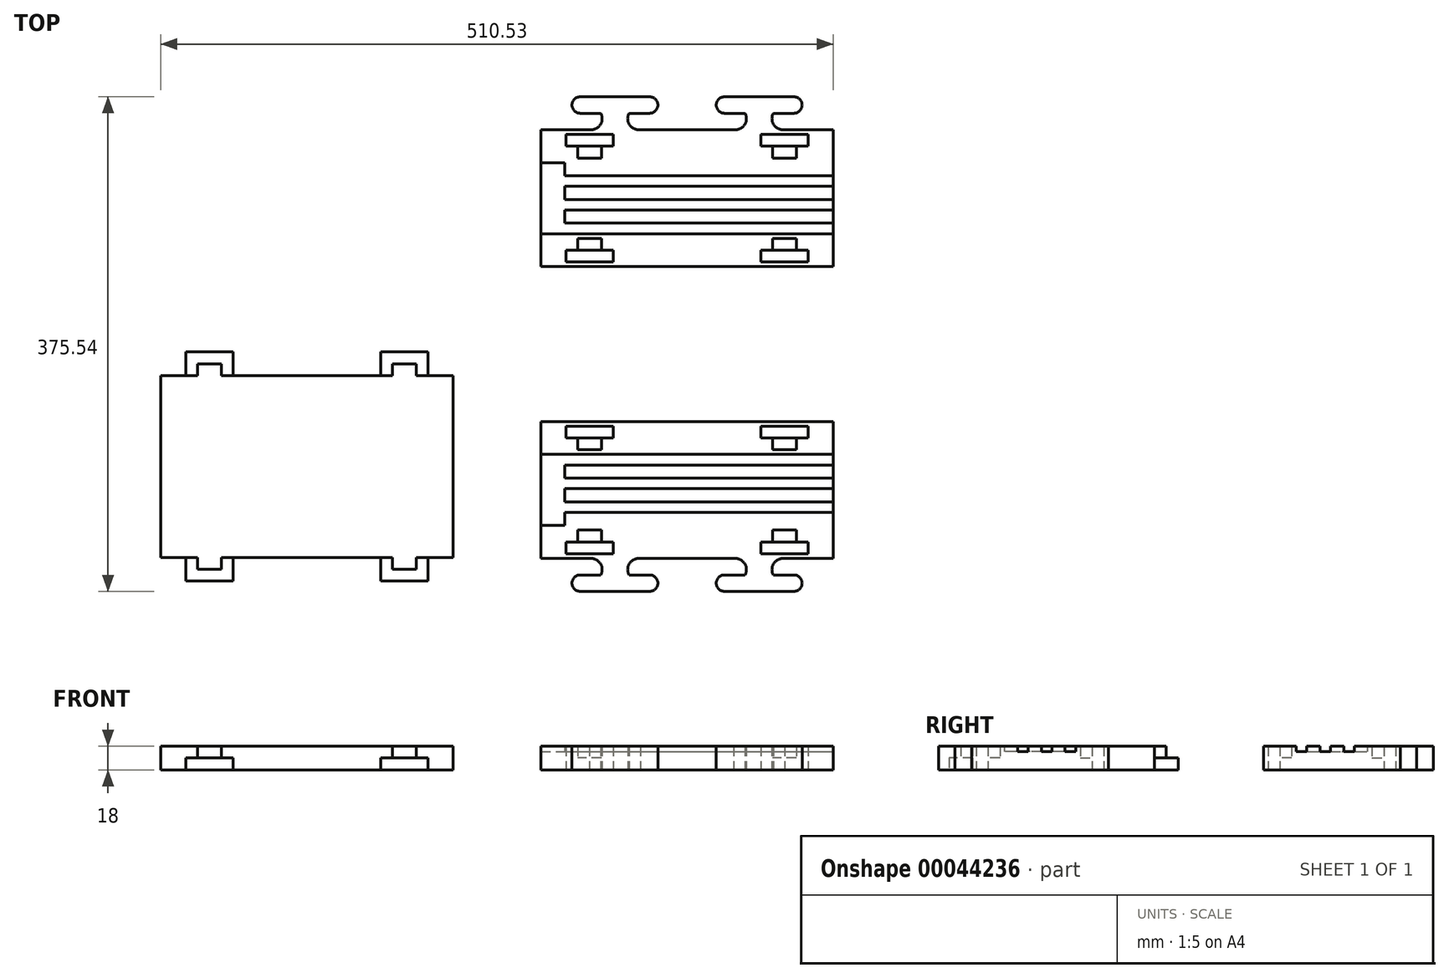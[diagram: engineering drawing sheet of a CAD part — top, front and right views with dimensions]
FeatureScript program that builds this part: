
annotation { "Feature Type Name" : "Feature", "Feature Type Description" : "" }
export const myFeature = defineFeature(function(context is Context, id is Id, definition is map)
    precondition{}
    {
        {
            var Q0;
            Q0=qCreatedBy(makeId("Top.planeOp"),FACE);
            var sketch = newSketch(context, id + "F0", { "sketchPlane" : qUnion([Q0])});
            skLineSegment(sketch, "E0.bottom", {"start": v(102.08, 91.5) * mm, "end": v(176.08, 91.5) * mm});
            skLineSegment(sketch, "E0.left", {"start": v(28.08, 91.5) * mm, "end": v(28.08, -12.5) * mm});
            skLineSegment(sketch, "E0.right", {"start": v(250.08, 91.5) * mm, "end": v(250.08, -12.5) * mm});
            skPoint(sketch, "E1", {"position": v(28.08, 66.5) * mm});
            skPoint(sketch, "E2", {"position": v(28.08, 12.5) * mm});
            skPoint(sketch, "E3", {"position": v(28.08, 58.5) * mm});
            skPoint(sketch, "E4", {"position": v(28.08, 22.5) * mm});
            skPoint(sketch, "E5", {"position": v(28.08, 48.5) * mm});
            skPoint(sketch, "E6", {"position": v(29.26, 40.5) * mm});
            skPoint(sketch, "E7", {"position": v(28.08, 30.5) * mm});
            skLineSegment(sketch, "E8", {"start": v(28.08, 66.5) * mm, "end": v(250.08, 66.5) * mm});
            skLineSegment(sketch, "E9", {"start": v(28.08, 48.5) * mm, "end": v(250.08, 48.5) * mm});
            skLineSegment(sketch, "E10", {"start": v(28.08, 30.5) * mm, "end": v(250.08, 30.5) * mm});
            skLineSegment(sketch, "E11", {"start": v(28.08, 12.5) * mm, "end": v(250.08, 12.5) * mm});
            skPoint(sketch, "E12", {"position": v(102.08, 91.5) * mm});
            skPoint(sketch, "E13", {"position": v(176.08, 91.5) * mm});
            skLineSegment(sketch, "E14", {"start": v(102.08, 91.5) * mm, "end": v(102.08, -12.5) * mm, "construction": true});
            skLineSegment(sketch, "E15", {"start": v(176.08, 91.5) * mm, "end": v(176.08, -12.5) * mm, "construction": true});
            skPoint(sketch, "E16", {"position": v(46.08, 66.5) * mm});
            skLineSegment(sketch, "E17", {"start": v(46.08, 66.5) * mm, "end": v(46.08, 12.5) * mm, "construction": true});
            skPoint(sketch, "E18", {"position": v(46.08, 58.5) * mm});
            skPoint(sketch, "E19", {"position": v(46.08, 40.5) * mm});
            skPoint(sketch, "E20", {"position": v(46.08, 22.5) * mm});
            skLineSegment(sketch, "E21", {"start": v(46.08, 40.5) * mm, "end": v(250.08, 40.5) * mm});
            skLineSegment(sketch, "E22", {"start": v(46.08, 58.5) * mm, "end": v(250.08, 58.5) * mm});
            skLineSegment(sketch, "E23", {"start": v(46.08, 22.5) * mm, "end": v(250.08, 22.5) * mm});
            skLineSegment(sketch, "E24", {"start": v(28.08, -12.5) * mm, "end": v(67.03, -12.5) * mm});
            skLineSegment(sketch, "E25", {"start": v(250.08, 91.5) * mm, "end": v(176.08, 91.5) * mm});
            skLineSegment(sketch, "E26", {"start": v(102.08, 91.5) * mm, "end": v(28.08, 91.5) * mm});
            skPoint(sketch, "E27", {"position": v(213.08, 91.5) * mm});
            skPoint(sketch, "E28", {"position": v(65.08, 91.5) * mm});
            skLineSegment(sketch, "E29", {"start": v(65.08, 91.5) * mm, "end": v(65.08, -12.5) * mm, "construction": true});
            skLineSegment(sketch, "E30", {"start": v(213.08, 91.5) * mm, "end": v(213.08, -12.5) * mm, "construction": true});
            skPoint(sketch, "E31", {"position": v(65.08, -9) * mm});
            skPoint(sketch, "E32", {"position": v(65.08, 88) * mm});
            skPoint(sketch, "E33", {"position": v(213.08, 88) * mm});
            skPoint(sketch, "E34", {"position": v(213.08, -9) * mm});
            skLineSegment(sketch, "E35", {"start": v(213.08, -9) * mm, "end": v(231.08, -9) * mm});
            skLineSegment(sketch, "E36", {"start": v(213.08, -9) * mm, "end": v(195.08, -9) * mm});
            skLineSegment(sketch, "E37", {"start": v(213.08, 88) * mm, "end": v(195.08, 88) * mm});
            skLineSegment(sketch, "E38", {"start": v(213.08, 88) * mm, "end": v(231.08, 88) * mm});
            skLineSegment(sketch, "E39", {"start": v(65.08, 88) * mm, "end": v(83.08, 88) * mm});
            skLineSegment(sketch, "E40", {"start": v(65.08, 88) * mm, "end": v(47.08, 88) * mm});
            skLineSegment(sketch, "E41", {"start": v(65.08, -9) * mm, "end": v(47.08, -9) * mm});
            skLineSegment(sketch, "E42", {"start": v(65.08, -9) * mm, "end": v(83.08, -9) * mm});
            skLineSegment(sketch, "E43", {"start": v(195.08, -9) * mm, "end": v(195.08, 0) * mm});
            skLineSegment(sketch, "E44", {"start": v(195.08, 88) * mm, "end": v(195.08, 79) * mm});
            skLineSegment(sketch, "E45", {"start": v(83.08, 88) * mm, "end": v(83.08, 79) * mm});
            skLineSegment(sketch, "E46", {"start": v(83.08, -9) * mm, "end": v(83.08, 0) * mm});
            skLineSegment(sketch, "E47", {"start": v(195.08, 0) * mm, "end": v(231.08, 0) * mm});
            skLineSegment(sketch, "E48", {"start": v(231.08, 0) * mm, "end": v(231.08, -9) * mm});
            skLineSegment(sketch, "E49", {"start": v(195.08, 79) * mm, "end": v(231.08, 79) * mm});
            skLineSegment(sketch, "E50", {"start": v(231.08, 79) * mm, "end": v(231.08, 88) * mm});
            skLineSegment(sketch, "E51", {"start": v(83.08, 79) * mm, "end": v(47.08, 79) * mm});
            skLineSegment(sketch, "E52", {"start": v(47.08, 79) * mm, "end": v(47.08, 88) * mm});
            skLineSegment(sketch, "E53", {"start": v(47.08, -9) * mm, "end": v(47.08, 0) * mm});
            skLineSegment(sketch, "E54", {"start": v(47.08, 0) * mm, "end": v(83.08, 0) * mm});
            skPoint(sketch, "E55", {"position": v(65.08, 70) * mm});
            skPoint(sketch, "E56", {"position": v(65.08, 9) * mm});
            skPoint(sketch, "E57", {"position": v(213.08, 9) * mm});
            skPoint(sketch, "E58", {"position": v(213.08, 70) * mm});
            skLineSegment(sketch, "E59", {"start": v(213.08, 9) * mm, "end": v(222.08, 9) * mm});
            skLineSegment(sketch, "E60", {"start": v(213.08, 9) * mm, "end": v(204.08, 9) * mm});
            skLineSegment(sketch, "E61", {"start": v(213.08, 70) * mm, "end": v(222.08, 70) * mm});
            skLineSegment(sketch, "E62", {"start": v(213.08, 70) * mm, "end": v(204.08, 70) * mm});
            skLineSegment(sketch, "E63", {"start": v(65.08, 70) * mm, "end": v(74.08, 70) * mm});
            skLineSegment(sketch, "E64", {"start": v(65.08, 70) * mm, "end": v(56.08, 70) * mm});
            skLineSegment(sketch, "E65", {"start": v(65.08, 9) * mm, "end": v(74.08, 9) * mm});
            skLineSegment(sketch, "E66", {"start": v(65.08, 9) * mm, "end": v(56.08, 9) * mm});
            skLineSegment(sketch, "E67", {"start": v(222.08, 9) * mm, "end": v(222.08, 0) * mm});
            skLineSegment(sketch, "E68", {"start": v(204.08, 9) * mm, "end": v(204.08, 0) * mm});
            skLineSegment(sketch, "E69", {"start": v(222.08, 70) * mm, "end": v(222.08, 79) * mm});
            skLineSegment(sketch, "E70", {"start": v(204.08, 70) * mm, "end": v(204.08, 79) * mm});
            skLineSegment(sketch, "E71", {"start": v(74.08, 70) * mm, "end": v(74.08, 79) * mm});
            skLineSegment(sketch, "E72", {"start": v(56.08, 70) * mm, "end": v(56.08, 79) * mm});
            skLineSegment(sketch, "E73", {"start": v(74.08, 9) * mm, "end": v(74.08, 0) * mm});
            skLineSegment(sketch, "E74", {"start": v(56.08, 9) * mm, "end": v(56.08, 0) * mm});
            skLineSegment(sketch, "E75", {"start": v(46.08, 58.5) * mm, "end": v(46.08, 48.5) * mm});
            skLineSegment(sketch, "E76", {"start": v(46.08, 40.5) * mm, "end": v(46.08, 30.5) * mm});
            skLineSegment(sketch, "E77", {"start": v(46.08, 22.5) * mm, "end": v(46.08, 12.5) * mm});
            skPoint(sketch, "E78", {"position": v(139.08, 91.5) * mm});
            skLineSegment(sketch, "E79", {"start": v(139.08, 91.5) * mm, "end": v(139.08, -12.5) * mm, "construction": true});
            skLineSegment(sketch, "E80.trimOffspring", {"start": v(119.85, -12.5) * mm, "end": v(158.31, -12.5) * mm});
            skLineSegment(sketch, "E81.trimOffspring", {"start": v(211.13, -12.5) * mm, "end": v(250.08, -12.5) * mm});
            skLineSegment(sketch, "E82", {"start": v(101.6, -12.5) * mm, "end": v(102.08, -12.5) * mm});
            skLineSegment(sketch, "E83", {"start": v(119.85, -12.5) * mm, "end": v(102.08, -12.5) * mm});
            skLineSegment(sketch, "E84", {"start": v(158.31, -12.5) * mm, "end": v(176.08, -12.5) * mm});
            skLineSegment(sketch, "E85", {"start": v(176.57, -12.5) * mm, "end": v(176.08, -12.5) * mm});
            skLineSegment(sketch, "E86", {"start": v(193.85, -12.5) * mm, "end": v(193.85, -37.5) * mm, "construction": true});
            skLineSegment(sketch, "E87", {"start": v(84.31, -12.5) * mm, "end": v(84.31, -37.5) * mm, "construction": true});
            skLineSegment(sketch, "E88", {"start": v(84.31, -25) * mm, "end": v(193.85, -25) * mm, "construction": true});
            skLineSegment(sketch, "E89", {"start": v(84.31, -25) * mm, "end": v(31.64, -25) * mm, "construction": true});
            skLineSegment(sketch, "E90", {"start": v(193.85, -25) * mm, "end": v(246.52, -25) * mm, "construction": true});
            skArc(sketch, "E91", {"start": v(213.08, -12.5) * mm, "mid": v(205.04, -16.17) * mm, "end": v(204.52, -25) * mm});
            skArc(sketch, "E92.MirrorCS", {"start": v(174.62, -12.5) * mm, "mid": v(182.66, -16.17) * mm, "end": v(183.17, -25) * mm});
            skArc(sketch, "E93.MirrorCS", {"start": v(103.55, -12.5) * mm, "mid": v(95.5, -16.17) * mm, "end": v(94.99, -25) * mm});
            skArc(sketch, "E94.MirrorCS", {"start": v(65.08, -12.5) * mm, "mid": v(73.13, -16.17) * mm, "end": v(73.64, -25) * mm});
            skLineSegment(sketch, "E95", {"start": v(73.64, -25) * mm, "end": v(57.98, -25) * mm});
            skLineSegment(sketch, "E96", {"start": v(94.99, -25) * mm, "end": v(110.65, -25) * mm});
            skLineSegment(sketch, "E97", {"start": v(183.17, -25) * mm, "end": v(167.51, -25) * mm});
            skLineSegment(sketch, "E98", {"start": v(204.52, -25) * mm, "end": v(220.18, -25) * mm});
            skArc(sketch, "E99", {"start": v(57.98, -25) * mm, "mid": v(51.73, -31.25) * mm, "end": v(57.98, -37.5) * mm});
            skArc(sketch, "E100.MirrorCS", {"start": v(110.65, -25) * mm, "mid": v(116.9, -31.25) * mm, "end": v(110.65, -37.5) * mm});
            skArc(sketch, "E101.MirrorCS", {"start": v(167.51, -25) * mm, "mid": v(161.26, -31.25) * mm, "end": v(167.51, -37.5) * mm});
            skArc(sketch, "E102.MirrorCS", {"start": v(220.18, -25) * mm, "mid": v(226.43, -31.25) * mm, "end": v(220.18, -37.5) * mm});
            skLineSegment(sketch, "E103", {"start": v(57.98, -37.5) * mm, "end": v(110.65, -37.5) * mm});
            skLineSegment(sketch, "E104", {"start": v(167.51, -37.5) * mm, "end": v(220.18, -37.5) * mm});
            skLineSegment(sketch, "E105", {"start": v(-11.33, 150.27) * mm, "end": v(328.55, 150.27) * mm});
            skLineSegment(sketch, "E106.MirrorCS", {"start": v(176.57, 313.04) * mm, "end": v(176.08, 313.04) * mm});
            skLineSegment(sketch, "E107.MirrorCS", {"start": v(231.08, 221.54) * mm, "end": v(231.08, 212.54) * mm});
            skLineSegment(sketch, "E108.MirrorCS", {"start": v(213.08, 230.54) * mm, "end": v(204.08, 230.54) * mm});
            skLineSegment(sketch, "E109.MirrorCS", {"start": v(83.08, 212.54) * mm, "end": v(83.08, 221.54) * mm});
            skLineSegment(sketch, "E110.MirrorCS", {"start": v(65.08, 291.54) * mm, "end": v(56.08, 291.54) * mm});
            skLineSegment(sketch, "E111.MirrorCS", {"start": v(47.08, 221.54) * mm, "end": v(47.08, 212.54) * mm});
            skLineSegment(sketch, "E112.MirrorCS", {"start": v(195.08, 212.54) * mm, "end": v(195.08, 221.54) * mm});
            skLineSegment(sketch, "E113.MirrorCS", {"start": v(213.08, 291.54) * mm, "end": v(204.08, 291.54) * mm});
            skLineSegment(sketch, "E114.MirrorCS", {"start": v(65.08, 230.54) * mm, "end": v(56.08, 230.54) * mm});
            skLineSegment(sketch, "E115.MirrorCS", {"start": v(74.08, 291.54) * mm, "end": v(74.08, 300.54) * mm});
            skLineSegment(sketch, "E116.MirrorCS", {"start": v(65.08, 291.54) * mm, "end": v(74.08, 291.54) * mm});
            skLineSegment(sketch, "E117.MirrorCS", {"start": v(204.08, 291.54) * mm, "end": v(204.08, 300.54) * mm});
            skLineSegment(sketch, "E118.MirrorCS", {"start": v(213.08, 230.54) * mm, "end": v(222.08, 230.54) * mm});
            skLineSegment(sketch, "E119.MirrorCS", {"start": v(46.08, 242.04) * mm, "end": v(46.08, 252.04) * mm});
            skLineSegment(sketch, "E120.MirrorCS", {"start": v(83.08, 309.54) * mm, "end": v(83.08, 300.54) * mm});
            skLineSegment(sketch, "E121.MirrorCS", {"start": v(222.08, 291.54) * mm, "end": v(222.08, 300.54) * mm});
            skLineSegment(sketch, "E122.MirrorCS", {"start": v(46.08, 278.04) * mm, "end": v(46.08, 288.04) * mm});
            skLineSegment(sketch, "E123.MirrorCS", {"start": v(46.08, 260.04) * mm, "end": v(46.08, 270.04) * mm});
            skLineSegment(sketch, "E124.MirrorCS", {"start": v(56.08, 291.54) * mm, "end": v(56.08, 300.54) * mm});
            skLineSegment(sketch, "E125.MirrorCS", {"start": v(65.08, 230.54) * mm, "end": v(74.08, 230.54) * mm});
            skLineSegment(sketch, "E126.MirrorCS", {"start": v(46.08, 234.04) * mm, "end": v(46.08, 288.04) * mm, "construction": true});
            skLineSegment(sketch, "E127.MirrorCS", {"start": v(213.08, 291.54) * mm, "end": v(222.08, 291.54) * mm});
            skPoint(sketch, "E128.MirrorP", {"position": v(213.08, 212.54) * mm});
            skLineSegment(sketch, "E129.MirrorCS", {"start": v(250.08, 209.04) * mm, "end": v(250.08, 313.04) * mm});
            skPoint(sketch, "E130.MirrorP", {"position": v(46.08, 234.04) * mm});
            skArc(sketch, "E131.MirrorCS", {"start": v(65.08, 313.04) * mm, "mid": v(73.13, 316.7) * mm, "end": v(73.64, 325.54) * mm});
            skLineSegment(sketch, "E132.MirrorCS", {"start": v(28.08, 252.04) * mm, "end": v(250.08, 252.04) * mm});
            skLineSegment(sketch, "E133.MirrorCS", {"start": v(65.08, 212.54) * mm, "end": v(83.08, 212.54) * mm});
            skLineSegment(sketch, "E134.MirrorCS", {"start": v(167.51, 338.04) * mm, "end": v(220.18, 338.04) * mm});
            skLineSegment(sketch, "E135.MirrorCS", {"start": v(84.31, 325.54) * mm, "end": v(193.85, 325.54) * mm, "construction": true});
            skLineSegment(sketch, "E136.MirrorCS", {"start": v(28.08, 313.04) * mm, "end": v(67.03, 313.04) * mm});
            skArc(sketch, "E137.MirrorCS", {"start": v(103.55, 313.04) * mm, "mid": v(95.5, 316.7) * mm, "end": v(94.99, 325.54) * mm});
            skArc(sketch, "E138.MirrorCS", {"start": v(57.98, 325.54) * mm, "mid": v(51.73, 331.79) * mm, "end": v(57.98, 338.04) * mm});
            skLineSegment(sketch, "E139.MirrorCS", {"start": v(139.08, 209.04) * mm, "end": v(139.08, 313.04) * mm, "construction": true});
            skLineSegment(sketch, "E140.MirrorCS", {"start": v(65.08, 309.54) * mm, "end": v(47.08, 309.54) * mm});
            skPoint(sketch, "E141.MirrorP", {"position": v(28.08, 278.04) * mm});
            skPoint(sketch, "E142.MirrorP", {"position": v(46.08, 278.04) * mm});
            skPoint(sketch, "E143.MirrorP", {"position": v(213.08, 209.04) * mm});
            skPoint(sketch, "E144.MirrorP", {"position": v(213.08, 230.54) * mm});
            skPoint(sketch, "E145.MirrorP", {"position": v(28.08, 270.04) * mm});
            skPoint(sketch, "E146.MirrorP", {"position": v(65.08, 209.04) * mm});
            skPoint(sketch, "E147.MirrorP", {"position": v(28.08, 252.04) * mm});
            skArc(sketch, "E148.MirrorCS", {"start": v(213.08, 313.04) * mm, "mid": v(205.04, 316.7) * mm, "end": v(204.52, 325.54) * mm});
            skPoint(sketch, "E149.MirrorP", {"position": v(65.08, 212.54) * mm});
            skArc(sketch, "E150.MirrorCS", {"start": v(167.51, 325.54) * mm, "mid": v(161.26, 331.79) * mm, "end": v(167.51, 338.04) * mm});
            skLineSegment(sketch, "E151.MirrorCS", {"start": v(119.85, 313.04) * mm, "end": v(158.31, 313.04) * mm});
            skArc(sketch, "E152.MirrorCS", {"start": v(174.62, 313.04) * mm, "mid": v(182.66, 316.7) * mm, "end": v(183.17, 325.54) * mm});
            skLineSegment(sketch, "E153.MirrorCS", {"start": v(176.08, 209.04) * mm, "end": v(176.08, 313.04) * mm, "construction": true});
            skLineSegment(sketch, "E154.MirrorCS", {"start": v(102.08, 209.04) * mm, "end": v(102.08, 313.04) * mm, "construction": true});
            skPoint(sketch, "E155.MirrorP", {"position": v(46.08, 260.04) * mm});
            skLineSegment(sketch, "E156.MirrorCS", {"start": v(213.08, 209.04) * mm, "end": v(213.08, 313.04) * mm, "construction": true});
            skLineSegment(sketch, "E157.MirrorCS", {"start": v(57.98, 338.04) * mm, "end": v(110.65, 338.04) * mm});
            skLineSegment(sketch, "E158.MirrorCS", {"start": v(84.31, 313.04) * mm, "end": v(84.31, 338.04) * mm, "construction": true});
            skArc(sketch, "E159.MirrorCS", {"start": v(220.18, 325.54) * mm, "mid": v(226.43, 331.79) * mm, "end": v(220.18, 338.04) * mm});
            skLineSegment(sketch, "E160.MirrorCS", {"start": v(47.08, 309.54) * mm, "end": v(47.08, 300.54) * mm});
            skPoint(sketch, "E161.MirrorP", {"position": v(65.08, 309.54) * mm});
            skPoint(sketch, "E162.MirrorP", {"position": v(139.08, 209.04) * mm});
            skLineSegment(sketch, "E163.MirrorCS", {"start": v(183.17, 325.54) * mm, "end": v(167.51, 325.54) * mm});
            skPoint(sketch, "E164.MirrorP", {"position": v(65.08, 291.54) * mm});
            skLineSegment(sketch, "E165.MirrorCS", {"start": v(73.64, 325.54) * mm, "end": v(57.98, 325.54) * mm});
            skLineSegment(sketch, "E166.MirrorCS", {"start": v(213.08, 212.54) * mm, "end": v(195.08, 212.54) * mm});
            skPoint(sketch, "E167.MirrorP", {"position": v(28.08, 234.04) * mm});
            skLineSegment(sketch, "E168.MirrorCS", {"start": v(28.08, 234.04) * mm, "end": v(250.08, 234.04) * mm});
            skPoint(sketch, "E169.MirrorP", {"position": v(176.08, 209.04) * mm});
            skPoint(sketch, "E170.MirrorP", {"position": v(213.08, 309.54) * mm});
            skLineSegment(sketch, "E171.MirrorCS", {"start": v(28.08, 209.04) * mm, "end": v(28.08, 313.04) * mm});
            skLineSegment(sketch, "E172.MirrorCS", {"start": v(119.85, 313.04) * mm, "end": v(102.08, 313.04) * mm});
            skLineSegment(sketch, "E173.MirrorCS", {"start": v(102.08, 209.04) * mm, "end": v(176.08, 209.04) * mm});
            skLineSegment(sketch, "E174.MirrorCS", {"start": v(193.85, 313.04) * mm, "end": v(193.85, 338.04) * mm, "construction": true});
            skPoint(sketch, "E175.MirrorP", {"position": v(46.08, 242.04) * mm});
            skLineSegment(sketch, "E176.MirrorCS", {"start": v(204.52, 325.54) * mm, "end": v(220.18, 325.54) * mm});
            skPoint(sketch, "E177.MirrorP", {"position": v(29.26, 260.04) * mm});
            skLineSegment(sketch, "E178.MirrorCS", {"start": v(193.85, 325.54) * mm, "end": v(246.52, 325.54) * mm, "construction": true});
            skArc(sketch, "E179.MirrorCS", {"start": v(110.65, 325.54) * mm, "mid": v(116.9, 331.79) * mm, "end": v(110.65, 338.04) * mm});
            skLineSegment(sketch, "E180.MirrorCS", {"start": v(213.08, 212.54) * mm, "end": v(231.08, 212.54) * mm});
            skLineSegment(sketch, "E181.MirrorCS", {"start": v(46.08, 278.04) * mm, "end": v(250.08, 278.04) * mm});
            skLineSegment(sketch, "E182.MirrorCS", {"start": v(213.08, 309.54) * mm, "end": v(231.08, 309.54) * mm});
            skLineSegment(sketch, "E183.MirrorCS", {"start": v(94.99, 325.54) * mm, "end": v(110.65, 325.54) * mm});
            skLineSegment(sketch, "E184.MirrorCS", {"start": v(56.08, 230.54) * mm, "end": v(56.08, 221.54) * mm});
            skLineSegment(sketch, "E185.MirrorCS", {"start": v(204.08, 230.54) * mm, "end": v(204.08, 221.54) * mm});
            skLineSegment(sketch, "E186.MirrorCS", {"start": v(46.08, 242.04) * mm, "end": v(250.08, 242.04) * mm});
            skLineSegment(sketch, "E187.MirrorCS", {"start": v(74.08, 230.54) * mm, "end": v(74.08, 221.54) * mm});
            skLineSegment(sketch, "E188.MirrorCS", {"start": v(102.08, 209.04) * mm, "end": v(28.08, 209.04) * mm});
            skLineSegment(sketch, "E189.MirrorCS", {"start": v(213.08, 309.54) * mm, "end": v(195.08, 309.54) * mm});
            skLineSegment(sketch, "E190.MirrorCS", {"start": v(84.31, 325.54) * mm, "end": v(31.64, 325.54) * mm, "construction": true});
            skLineSegment(sketch, "E191.MirrorCS", {"start": v(46.08, 260.04) * mm, "end": v(250.08, 260.04) * mm});
            skLineSegment(sketch, "E192.MirrorCS", {"start": v(158.31, 313.04) * mm, "end": v(176.08, 313.04) * mm});
            skPoint(sketch, "E193.MirrorP", {"position": v(28.08, 288.04) * mm});
            skLineSegment(sketch, "E194.MirrorCS", {"start": v(195.08, 221.54) * mm, "end": v(231.08, 221.54) * mm});
            skLineSegment(sketch, "E195.MirrorCS", {"start": v(195.08, 309.54) * mm, "end": v(195.08, 300.54) * mm});
            skLineSegment(sketch, "E196.MirrorCS", {"start": v(65.08, 309.54) * mm, "end": v(83.08, 309.54) * mm});
            skLineSegment(sketch, "E197.MirrorCS", {"start": v(47.08, 300.54) * mm, "end": v(83.08, 300.54) * mm});
            skLineSegment(sketch, "E198.MirrorCS", {"start": v(65.08, 209.04) * mm, "end": v(65.08, 313.04) * mm, "construction": true});
            skPoint(sketch, "E199.MirrorP", {"position": v(65.08, 230.54) * mm});
            skLineSegment(sketch, "E200.MirrorCS", {"start": v(28.08, 288.04) * mm, "end": v(250.08, 288.04) * mm});
            skLineSegment(sketch, "E201.MirrorCS", {"start": v(231.08, 300.54) * mm, "end": v(231.08, 309.54) * mm});
            skLineSegment(sketch, "E202.MirrorCS", {"start": v(195.08, 300.54) * mm, "end": v(231.08, 300.54) * mm});
            skLineSegment(sketch, "E203.MirrorCS", {"start": v(28.08, 270.04) * mm, "end": v(250.08, 270.04) * mm});
            skPoint(sketch, "E204.MirrorP", {"position": v(213.08, 291.54) * mm});
            skPoint(sketch, "E205.MirrorP", {"position": v(102.08, 209.04) * mm});
            skLineSegment(sketch, "E206.MirrorCS", {"start": v(211.13, 313.04) * mm, "end": v(250.08, 313.04) * mm});
            skLineSegment(sketch, "E207.MirrorCS", {"start": v(250.08, 209.04) * mm, "end": v(176.08, 209.04) * mm});
            skLineSegment(sketch, "E208.MirrorCS", {"start": v(65.08, 212.54) * mm, "end": v(47.08, 212.54) * mm});
            skPoint(sketch, "E209.MirrorP", {"position": v(28.08, 242.04) * mm});
            skLineSegment(sketch, "E210.MirrorCS", {"start": v(222.08, 230.54) * mm, "end": v(222.08, 221.54) * mm});
            skLineSegment(sketch, "E211.MirrorCS", {"start": v(83.08, 221.54) * mm, "end": v(47.08, 221.54) * mm});
            skSolve(sketch);
        }
        {
            var Q0;
            Q0=qCreatedBy(makeId("Top.planeOp"),FACE);
            var sketch = newSketch(context, id + "F1", { "sketchPlane" : qUnion([Q0])});
            skLineSegment(sketch, "E212.bottom", {"start": v(-260.45, 126.28) * mm, "end": v(-186.45, 126.28) * mm});
            skLineSegment(sketch, "E212.top", {"start": v(-260.45, -11.72) * mm, "end": v(-38.45, -11.72) * mm});
            skLineSegment(sketch, "E212.left", {"start": v(-260.45, 126.28) * mm, "end": v(-260.45, -11.72) * mm});
            skLineSegment(sketch, "E212.right", {"start": v(-38.45, 126.28) * mm, "end": v(-38.45, -11.72) * mm});
            skPoint(sketch, "E213", {"position": v(-186.45, 126.28) * mm});
            skPoint(sketch, "E214", {"position": v(-112.45, 126.28) * mm});
            skLineSegment(sketch, "E215", {"start": v(-260.45, 57.28) * mm, "end": v(-38.45, 57.28) * mm, "construction": true});
            skLineSegment(sketch, "E216", {"start": v(-186.45, 126.28) * mm, "end": v(-186.45, -11.72) * mm, "construction": true});
            skLineSegment(sketch, "E217", {"start": v(-112.45, 126.28) * mm, "end": v(-112.45, -11.72) * mm, "construction": true});
            skLineSegment(sketch, "E218.trimOffspring", {"start": v(-112.45, 126.28) * mm, "end": v(-75.45, 126.28) * mm});
            skLineSegment(sketch, "E219", {"start": v(-112.45, 126.28) * mm, "end": v(-186.45, 126.28) * mm});
            skLineSegment(sketch, "E220", {"start": v(-149.45, 126.28) * mm, "end": v(-149.45, -11.72) * mm, "construction": true});
            skLineSegment(sketch, "E221", {"start": v(-223.45, 126.28) * mm, "end": v(-223.45, -11.72) * mm, "construction": true});
            skLineSegment(sketch, "E222", {"start": v(-75.45, 126.28) * mm, "end": v(-75.45, -11.72) * mm, "construction": true});
            skPoint(sketch, "E223", {"position": v(-57.45, 126.28) * mm});
            skLineSegment(sketch, "E224", {"start": v(-57.45, 126.28) * mm, "end": v(-57.45, 144.28) * mm});
            skLineSegment(sketch, "E225", {"start": v(-57.45, 144.28) * mm, "end": v(-75.45, 144.28) * mm});
            skLineSegment(sketch, "E226.trimOffspring", {"start": v(-57.45, 126.28) * mm, "end": v(-38.45, 126.28) * mm});
            skLineSegment(sketch, "E227", {"start": v(-57.45, 126.28) * mm, "end": v(-75.45, 126.28) * mm});
            skLineSegment(sketch, "E228", {"start": v(-66.45, 126.28) * mm, "end": v(-66.45, 135.28) * mm});
            skPoint(sketch, "E228.endSnap0", {"position": v(-57.45, 135.28) * mm});
            skLineSegment(sketch, "E229", {"start": v(-66.45, 135.28) * mm, "end": v(-75.45, 135.28) * mm});
            skLineSegment(sketch, "E230.MirrorCS", {"start": v(-66.45, -20.72) * mm, "end": v(-75.45, -20.72) * mm});
            skLineSegment(sketch, "E231.MirrorCS", {"start": v(-57.45, -29.72) * mm, "end": v(-75.45, -29.72) * mm});
            skLineSegment(sketch, "E232.MirrorCS", {"start": v(-57.45, -11.72) * mm, "end": v(-57.45, -29.72) * mm});
            skLineSegment(sketch, "E233.MirrorCS", {"start": v(-66.45, -11.72) * mm, "end": v(-66.45, -20.72) * mm});
            skLineSegment(sketch, "E234.MirrorCS", {"start": v(-232.45, 135.28) * mm, "end": v(-223.45, 135.28) * mm});
            skLineSegment(sketch, "E235.MirrorCS", {"start": v(-241.45, 144.28) * mm, "end": v(-223.45, 144.28) * mm});
            skLineSegment(sketch, "E236.MirrorCS", {"start": v(-241.45, 126.28) * mm, "end": v(-241.45, 144.28) * mm});
            skLineSegment(sketch, "E237.MirrorCS", {"start": v(-232.45, 126.28) * mm, "end": v(-232.45, 135.28) * mm});
            skLineSegment(sketch, "E238.MirrorCS", {"start": v(-232.45, -11.72) * mm, "end": v(-232.45, -20.72) * mm});
            skLineSegment(sketch, "E239.MirrorCS", {"start": v(-232.45, -20.72) * mm, "end": v(-223.45, -20.72) * mm});
            skLineSegment(sketch, "E240.MirrorCS", {"start": v(-241.45, -29.72) * mm, "end": v(-223.45, -29.72) * mm});
            skLineSegment(sketch, "E241.MirrorCS", {"start": v(-241.45, -11.72) * mm, "end": v(-241.45, -29.72) * mm});
            skLineSegment(sketch, "E242.MirrorCS", {"start": v(-84.45, 135.28) * mm, "end": v(-75.45, 135.28) * mm});
            skLineSegment(sketch, "E243.MirrorCS", {"start": v(-84.45, 126.28) * mm, "end": v(-84.45, 135.28) * mm});
            skLineSegment(sketch, "E244.MirrorCS", {"start": v(-93.45, 126.28) * mm, "end": v(-93.45, 144.28) * mm});
            skLineSegment(sketch, "E245.MirrorCS", {"start": v(-93.45, 144.28) * mm, "end": v(-75.45, 144.28) * mm});
            skLineSegment(sketch, "E246.MirrorCS", {"start": v(-84.45, -11.72) * mm, "end": v(-84.45, -20.72) * mm});
            skLineSegment(sketch, "E247.MirrorCS", {"start": v(-84.45, -20.72) * mm, "end": v(-75.45, -20.72) * mm});
            skLineSegment(sketch, "E248.MirrorCS", {"start": v(-93.45, -29.72) * mm, "end": v(-75.45, -29.72) * mm});
            skLineSegment(sketch, "E249.MirrorCS", {"start": v(-93.45, -11.72) * mm, "end": v(-93.45, -29.72) * mm});
            skLineSegment(sketch, "E250.MirrorCS", {"start": v(-214.45, 126.28) * mm, "end": v(-214.45, 135.28) * mm});
            skLineSegment(sketch, "E251.MirrorCS", {"start": v(-214.45, 135.28) * mm, "end": v(-223.45, 135.28) * mm});
            skLineSegment(sketch, "E252.MirrorCS", {"start": v(-205.45, 144.28) * mm, "end": v(-223.45, 144.28) * mm});
            skLineSegment(sketch, "E253.MirrorCS", {"start": v(-205.45, 126.28) * mm, "end": v(-205.45, 144.28) * mm});
            skLineSegment(sketch, "E254.MirrorCS", {"start": v(-205.45, -11.72) * mm, "end": v(-205.45, -29.72) * mm});
            skLineSegment(sketch, "E255.MirrorCS", {"start": v(-214.45, -11.72) * mm, "end": v(-214.45, -20.72) * mm});
            skLineSegment(sketch, "E256.MirrorCS", {"start": v(-214.45, -20.72) * mm, "end": v(-223.45, -20.72) * mm});
            skLineSegment(sketch, "E257.MirrorCS", {"start": v(-205.45, -29.72) * mm, "end": v(-223.45, -29.72) * mm});
            skSolve(sketch);
        }
        {
            var Q0;
            Q0=makeQuery(id+"F0.imprint","IMPRINT",FACE,{"disambiguationData":[TD([[makeQuery(id+"F0.imprint","IMPRINT",EDGE,{"derivedFrom":sQuery(id+"F0.wireOp",EDGE,"E35")}),-1.0]])]});
            var Q1;
            Q1=makeQuery(id+"F0.imprint","IMPRINT",FACE,{"disambiguationData":[TD([[makeQuery(id+"F0.imprint","IMPRINT",EDGE,{"derivedFrom":sQuery(id+"F0.wireOp",EDGE,"E0.bottom")}),-1.0]])]});
            var Q2;
            {var subQ3=sQuery(id+"F0.wireOp",EDGE,"E22");Q2=makeQuery(id+"F0.imprint","IMPRINT",FACE,{"disambiguationData":[TD([[makeQuery(id+"F0.imprint","IMPRINT",EDGE,{"derivedFrom":subQ3}),-1.0]])]});}
            var Q3;
            {var subQ3=sQuery(id+"F0.wireOp",EDGE,"E21");Q3=makeQuery(id+"F0.imprint","IMPRINT",FACE,{"disambiguationData":[TD([[makeQuery(id+"F0.imprint","IMPRINT",EDGE,{"derivedFrom":subQ3}),-1.0]])]});}
            var Q4;
            {var subQ3=sQuery(id+"F0.wireOp",EDGE,"E23");Q4=makeQuery(id+"F0.imprint","IMPRINT",FACE,{"disambiguationData":[TD([[makeQuery(id+"F0.imprint","IMPRINT",EDGE,{"derivedFrom":subQ3}),-1.0]])]});}
            var Q5;
            {var subQ6=sQuery(id+"F0.wireOp",EDGE,"E107.MirrorCS");Q5=makeQuery(id+"F0.imprint","IMPRINT",FACE,{"disambiguationData":[TD([[makeQuery(id+"F0.imprint","IMPRINT",EDGE,{"derivedFrom":subQ6}),1.0]])]});}
            var Q6;
            {var subQ0=sQuery(id+"F0.wireOp",EDGE,"E119.MirrorCS");Q6=makeQuery(id+"F0.imprint","IMPRINT",FACE,{"disambiguationData":[TD([[makeQuery(id+"F0.imprint","IMPRINT",EDGE,{"derivedFrom":subQ0}),-1.0]])]});}
            var Q7;
            {var subQ0=sQuery(id+"F0.wireOp",EDGE,"E123.MirrorCS");Q7=makeQuery(id+"F0.imprint","IMPRINT",FACE,{"disambiguationData":[TD([[makeQuery(id+"F0.imprint","IMPRINT",EDGE,{"derivedFrom":subQ0}),-1.0]])]});}
            var Q8;
            {var subQ0=sQuery(id+"F0.wireOp",EDGE,"E122.MirrorCS");Q8=makeQuery(id+"F0.imprint","IMPRINT",FACE,{"disambiguationData":[TD([[makeQuery(id+"F0.imprint","IMPRINT",EDGE,{"derivedFrom":subQ0}),-1.0]])]});}
            var Q9;
            Q9=makeQuery(id+"F0.imprint","IMPRINT",FACE,{"disambiguationData":[TD([[makeQuery(id+"F0.imprint","IMPRINT",EDGE,{"derivedFrom":sQuery(id+"F0.wireOp",EDGE,"E110.MirrorCS")}),1.0]])]});
            var Q10;
            {var subQ1=sQuery(id+"F1.wireOp",EDGE,"E212.left");Q10=makeQuery(id+"F1.imprint","IMPRINT",FACE,{"disambiguationData":[TD([[makeQuery(id+"F1.imprint","IMPRINT",EDGE,{"derivedFrom":subQ1}),1.0]])]});}
            var Q11;
            {var subQ0=sQuery(id+"F1.wireOp",EDGE,"E228");Q11=makeQuery(id+"F1.imprint","IMPRINT",FACE,{"disambiguationData":[TD([[makeQuery(id+"F1.imprint","IMPRINT",EDGE,{"derivedFrom":subQ0}),1.0]])]});}
            var Q12;
            Q12=makeQuery(id+"F1.imprint","IMPRINT",FACE,{"disambiguationData":[TD([[makeQuery(id+"F1.imprint","IMPRINT",EDGE,{"derivedFrom":sQuery(id+"F1.wireOp",EDGE,"E230.MirrorCS")}),-1.0]])]});
            var Q13;
            {var subQ1=sQuery(id+"F1.wireOp",EDGE,"E238.MirrorCS");Q13=makeQuery(id+"F1.imprint","IMPRINT",FACE,{"disambiguationData":[TD([[makeQuery(id+"F1.imprint","IMPRINT",EDGE,{"derivedFrom":subQ1}),1.0]])]});}
            var Q14;
            Q14=makeQuery(id+"F1.imprint","IMPRINT",FACE,{"disambiguationData":[TD([[makeQuery(id+"F1.imprint","IMPRINT",EDGE,{"derivedFrom":sQuery(id+"F1.wireOp",EDGE,"E234.MirrorCS")}),-1.0]])]});
            extrude(context, id + "F2", {"entities" : qUnion([Q0, Q1, Q2, Q3, Q4, Q5, Q6, Q7, Q8, Q9, Q10, Q11, Q12, Q13, Q14]), "depth" : 18 * mm});
        }
        {
            var Q0;
            Q0=makeQuery(id+"F0.imprint","IMPRINT",FACE,{"disambiguationData":[TD([[makeQuery(id+"F0.imprint","IMPRINT",EDGE,{"derivedFrom":sQuery(id+"F0.wireOp",EDGE,"E110.MirrorCS")}),-1.0]])]});
            var Q1;
            Q1=makeQuery(id+"F0.imprint","IMPRINT",FACE,{"disambiguationData":[TD([[makeQuery(id+"F0.imprint","IMPRINT",EDGE,{"derivedFrom":sQuery(id+"F0.wireOp",EDGE,"E114.MirrorCS")}),1.0]])]});
            var Q2;
            Q2=makeQuery(id+"F0.imprint","IMPRINT",FACE,{"disambiguationData":[TD([[makeQuery(id+"F0.imprint","IMPRINT",EDGE,{"derivedFrom":sQuery(id+"F0.wireOp",EDGE,"E108.MirrorCS")}),1.0]])]});
            var Q3;
            Q3=makeQuery(id+"F0.imprint","IMPRINT",FACE,{"disambiguationData":[TD([[makeQuery(id+"F0.imprint","IMPRINT",EDGE,{"derivedFrom":sQuery(id+"F0.wireOp",EDGE,"E113.MirrorCS")}),-1.0]])]});
            var Q4;
            Q4=makeQuery(id+"F0.imprint","IMPRINT",FACE,{"disambiguationData":[TD([[makeQuery(id+"F0.imprint","IMPRINT",EDGE,{"derivedFrom":sQuery(id+"F0.wireOp",EDGE,"E61")}),1.0]])]});
            var Q5;
            Q5=makeQuery(id+"F0.imprint","IMPRINT",FACE,{"disambiguationData":[TD([[makeQuery(id+"F0.imprint","IMPRINT",EDGE,{"derivedFrom":sQuery(id+"F0.wireOp",EDGE,"E63")}),1.0]])]});
            var Q6;
            Q6=makeQuery(id+"F0.imprint","IMPRINT",FACE,{"disambiguationData":[TD([[makeQuery(id+"F0.imprint","IMPRINT",EDGE,{"derivedFrom":sQuery(id+"F0.wireOp",EDGE,"E65")}),-1.0]])]});
            var Q7;
            Q7=makeQuery(id+"F0.imprint","IMPRINT",FACE,{"disambiguationData":[TD([[makeQuery(id+"F0.imprint","IMPRINT",EDGE,{"derivedFrom":sQuery(id+"F0.wireOp",EDGE,"E59")}),-1.0]])]});
            var Q8;
            {var subQ1=sQuery(id+"F1.wireOp",EDGE,"E224");Q8=makeQuery(id+"F1.imprint","IMPRINT",FACE,{"disambiguationData":[TD([[makeQuery(id+"F1.imprint","IMPRINT",EDGE,{"derivedFrom":subQ1}),1.0]])]});}
            var Q9;
            Q9=makeQuery(id+"F1.imprint","IMPRINT",FACE,{"disambiguationData":[TD([[makeQuery(id+"F1.imprint","IMPRINT",EDGE,{"derivedFrom":sQuery(id+"F1.wireOp",EDGE,"E234.MirrorCS")}),1.0]])]});
            var Q10;
            {var subQ0=sQuery(id+"F1.wireOp",EDGE,"E238.MirrorCS");Q10=makeQuery(id+"F1.imprint","IMPRINT",FACE,{"disambiguationData":[TD([[makeQuery(id+"F1.imprint","IMPRINT",EDGE,{"derivedFrom":subQ0}),-1.0]])]});}
            var Q11;
            Q11=makeQuery(id+"F1.imprint","IMPRINT",FACE,{"disambiguationData":[TD([[makeQuery(id+"F1.imprint","IMPRINT",EDGE,{"derivedFrom":sQuery(id+"F1.wireOp",EDGE,"E230.MirrorCS")}),1.0]])]});
            extrude(context, id + "F3", {"entities" : qUnion([Q0, Q1, Q2, Q3, Q4, Q5, Q6, Q7, Q8, Q9, Q10, Q11]), "operationType" : NewBodyOperationType.ADD, "depth" : 9 * mm});
        }
        {
            var Q0;
            {var subQ1=sQuery(id+"F0.wireOp",EDGE,"E119.MirrorCS");Q0=makeQuery(id+"F0.imprint","IMPRINT",FACE,{"disambiguationData":[TD([[makeQuery(id+"F0.imprint","IMPRINT",EDGE,{"derivedFrom":subQ1}),1.0]])]});}
            var Q1;
            {var subQ8=sQuery(id+"F0.wireOp",EDGE,"E123.MirrorCS");Q1=makeQuery(id+"F0.imprint","IMPRINT",FACE,{"disambiguationData":[TD([[makeQuery(id+"F0.imprint","IMPRINT",EDGE,{"derivedFrom":subQ8}),1.0]])]});}
            var Q2;
            {var subQ9=sQuery(id+"F0.wireOp",EDGE,"E122.MirrorCS");Q2=makeQuery(id+"F0.imprint","IMPRINT",FACE,{"disambiguationData":[TD([[makeQuery(id+"F0.imprint","IMPRINT",EDGE,{"derivedFrom":subQ9}),1.0]])]});}
            var Q3;
            {var subQ4=sQuery(id+"F0.wireOp",EDGE,"E8");Q3=makeQuery(id+"F0.imprint","IMPRINT",FACE,{"disambiguationData":[TD([[makeQuery(id+"F0.imprint","IMPRINT",EDGE,{"derivedFrom":subQ4}),-1.0]])]});}
            var Q4;
            {var subQ6=sQuery(id+"F0.wireOp",EDGE,"E21");Q4=makeQuery(id+"F0.imprint","IMPRINT",FACE,{"disambiguationData":[TD([[makeQuery(id+"F0.imprint","IMPRINT",EDGE,{"derivedFrom":subQ6}),1.0]])]});}
            var Q5;
            {var subQ6=sQuery(id+"F0.wireOp",EDGE,"E23");Q5=makeQuery(id+"F0.imprint","IMPRINT",FACE,{"disambiguationData":[TD([[makeQuery(id+"F0.imprint","IMPRINT",EDGE,{"derivedFrom":subQ6}),1.0]])]});}
            extrude(context, id + "F4", {"entities" : qUnion([Q0, Q1, Q2, Q3, Q4, Q5]), "operationType" : NewBodyOperationType.ADD, "depth" : 14 * mm});
        }
    });
